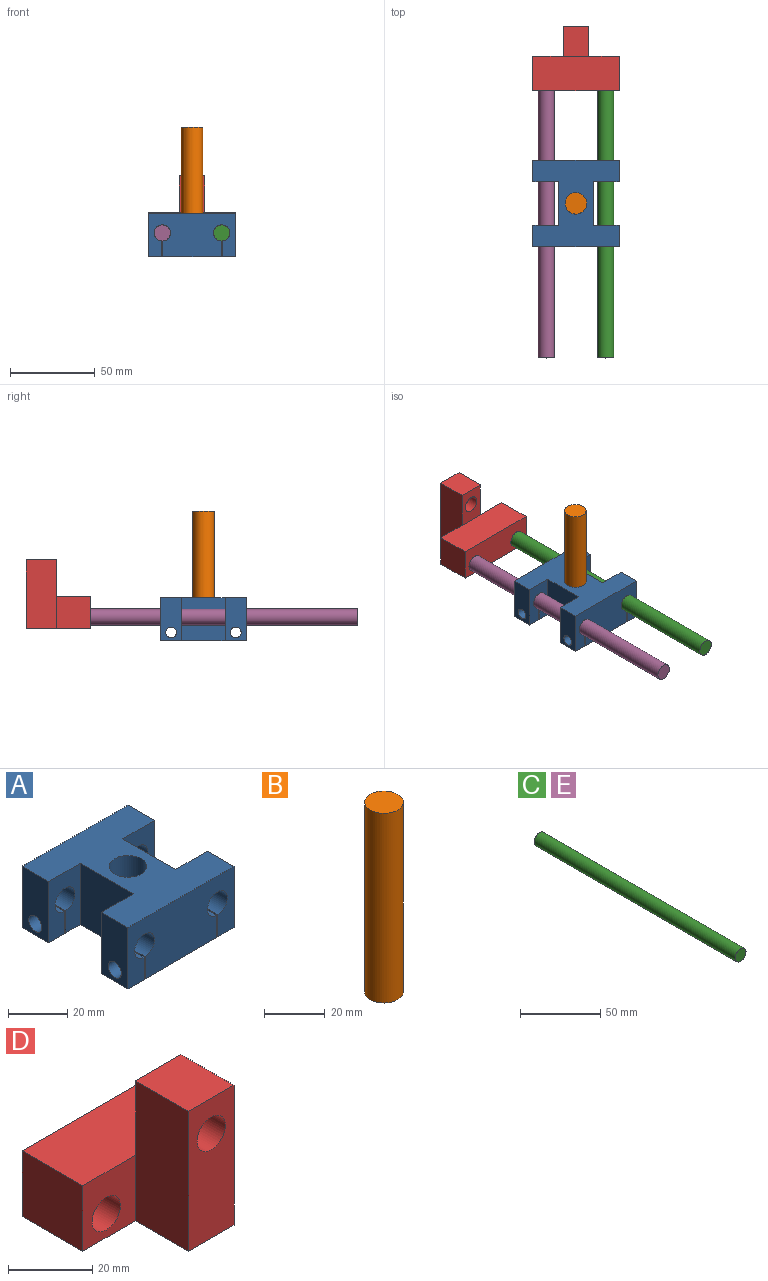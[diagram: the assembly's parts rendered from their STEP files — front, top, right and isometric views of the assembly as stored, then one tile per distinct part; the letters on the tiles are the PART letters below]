
ASSEMBLY  parts=5 mates=5
PART A: 37 faces, bbox 50.8x50.8x25.4 mm
  f0: plane 25.4x12.7mm, normal (1,0,0), area 290.9mm2, adj f8,f9,f22,f28,f36
  f1: plane 25.4x12.7mm, normal (-1,0,0), area 290.9mm2, adj f9,f20,f22,f26,f31
  f2: cylinder r=4.76mm len=12.7mm, axis (0,1,0), area 373.6mm2, adj f3,f11,f23,f27
  f3: plane 12.7x9.21mm, normal (-1,0,0), area 85.4mm2, adj f2,f4,f23,f27,f34
  f4: plane 50.8x34.42mm, normal (0,0,-1), area 1263.6mm2, adj f3,f5,f13,f14,f22,f23,f24,f25
  f5: plane 12.7x9.21mm, normal (1,0,0), area 85.4mm2, adj f4,f6,f22,f28,f35
  f6: cylinder r=4.76mm len=12.7mm, axis (0,1,0), area 373.6mm2, adj f5,f7,f22,f28
  f7: plane 12.7x9.21mm, normal (-1,0,0), area 85.4mm2, adj f6,f8,f22,f28,f36
  f8: plane 12.7x7.68mm, normal (0,0,-1), area 97.6mm2, adj f0,f7,f22,f28
  f9: plane 50.8x50.8mm, normal (0,0,1), area 1679.8mm2, adj f0,f1,f18,f19,f22,f23,f24,f25
  f10: plane 12.7x7.68mm, normal (0,0,-1), area 97.6mm2, adj f11,f19,f23,f27
  f11: plane 12.7x9.21mm, normal (1,0,0), area 85.4mm2, adj f2,f10,f23,f27,f32
  f12: cylinder r=4.76mm len=12.7mm, axis (0,1,0), area 373.6mm2, adj f13,f21,f22,f26
  f13: plane 12.7x9.21mm, normal (-1,0,0), area 85.4mm2, adj f4,f12,f22,f26,f35
  f14: plane 12.7x9.21mm, normal (1,0,0), area 85.4mm2, adj f4,f15,f23,f29,f34
  f15: cylinder r=4.76mm len=12.7mm, axis (0,1,0), area 373.6mm2, adj f14,f16,f23,f29
  f16: plane 12.7x9.21mm, normal (-1,0,0), area 85.4mm2, adj f15,f17,f23,f29,f33
  f17: plane 12.7x7.68mm, normal (0,0,-1), area 97.6mm2, adj f16,f18,f23,f29
  f18: plane 25.4x12.7mm, normal (1,0,0), area 290.9mm2, adj f9,f17,f23,f29,f33
  f19: plane 25.4x12.7mm, normal (-1,0,0), area 290.9mm2, adj f9,f10,f23,f27,f32
  f20: plane 12.7x7.68mm, normal (0,0,-1), area 97.6mm2, adj f1,f21,f22,f26
  f21: plane 12.7x9.21mm, normal (1,0,0), area 85.4mm2, adj f12,f20,f22,f26,f31
  f22: plane 50.8x25.4mm, normal (0,-1,0), area 1138.5mm2, adj f0,f1,f4,f5,f6,f7,f8,f9
  f23: plane 50.8x25.4mm, normal (0,1,0), area 1138.5mm2, adj f2,f3,f4,f9,f10,f11,f14,f15
  f24: cylinder r=6.35mm len=25.4mm, axis (0,0,1), area 1013.4mm2, adj f4,f9
  f25: plane 25.4x25.4mm, normal (-1,0,0), area 645.2mm2, adj f4,f9,f26,f27
  f26: plane 25.4x15.24mm, normal (0,1,0), area 311.2mm2, adj f1,f4,f9,f12,f13,f20,f21,f25
  f27: plane 25.4x15.24mm, normal (0,-1,0), area 311.2mm2, adj f2,f3,f4,f9,f10,f11,f19,f25
  f28: plane 25.4x15.24mm, normal (0,1,0), area 311.2mm2, adj f0,f4,f5,f6,f7,f8,f9,f30
  f29: plane 25.4x15.24mm, normal (0,-1,0), area 311.2mm2, adj f4,f9,f14,f15,f16,f17,f18,f30
  f30: plane 25.4x25.4mm, normal (1,0,0), area 645.2mm2, adj f4,f9,f28,f29
  f31: cylinder r=3.17mm len=7.68mm, axis (1,0,0), area 153.3mm2, adj f1,f21
  f32: cylinder r=3.17mm len=7.68mm, axis (1,0,0), area 153.3mm2, adj f11,f19
  f33: cylinder r=3.17mm len=7.68mm, axis (1,0,0), area 153.3mm2, adj f16,f18
  f34: cylinder r=3.17mm len=34.42mm, axis (1,0,0), area 686.6mm2, adj f3,f14
  f35: cylinder r=3.17mm len=34.42mm, axis (1,0,0), area 686.6mm2, adj f5,f13
  f36: cylinder r=3.17mm len=7.68mm, axis (1,0,0), area 153.3mm2, adj f0,f7
PART B: 3 faces, bbox 12.7x12.7x76.2 mm
  f0: cylinder r=6.35mm len=76.2mm, axis (0,0,-1), area 3040.2mm2, adj f1,f2
  f1: plane 12.7x12.7mm, normal (0,0,1), area 126.7mm2, adj f0
  f2: plane 12.7x12.7mm, normal (0,0,-1), area 126.7mm2, adj f0
PART C: 3 faces, bbox 9.5x177.8x9.5 mm
  f0: cylinder r=4.76mm len=177.8mm, axis (0,-1,0), area 5320.4mm2, adj f1,f2
  f1: plane 9.53x9.53mm, normal (0,1,0), area 71.3mm2, adj f0
  f2: plane 9.53x9.53mm, normal (0,-1,0), area 71.3mm2, adj f0
PART D: 15 faces, bbox 50.8x38.1x40.6 mm
  f0: plane 17.78x15.24mm, normal (0,0,1), area 271mm2, adj f1,f2,f11,f13
  f1: plane 40.64x15.24mm, normal (0,-1,0), area 548.1mm2, adj f0,f3,f7,f11,f13
  f2: plane 21.59x15.24mm, normal (0,1,0), area 257.8mm2, adj f0,f7,f10,f11,f13
  f3: plane 50.8x38.1mm, normal (0,0,-1), area 1303.2mm2, adj f1,f6,f8,f9,f11,f12,f13,f14
  f4: cylinder r=4.76mm len=20.32mm, axis (0,1,0), area 608mm2, adj f9,f14
  f5: cylinder r=4.76mm len=20.32mm, axis (0,1,0), area 608mm2, adj f9,f12
  f6: plane 20.32x19.05mm, normal (-1,0,0), area 387.1mm2, adj f3,f9,f10,f12
  f7: cylinder r=4.76mm len=17.78mm, axis (0,1,0), area 532mm2, adj f1,f2
  f8: plane 20.32x19.05mm, normal (1,0,0), area 387.1mm2, adj f3,f9,f10,f14
  f9: plane 50.8x19.05mm, normal (0,1,0), area 825.2mm2, adj f3,f4,f5,f6,f8,f10
  f10: plane 50.8x20.32mm, normal (0,0,1), area 1032.3mm2, adj f2,f6,f8,f9,f12,f14
  f11: plane 40.64x17.78mm, normal (-1,0,0), area 722.6mm2, adj f0,f1,f2,f3,f12
  f12: plane 19.05x17.78mm, normal (0,-1,0), area 267.5mm2, adj f3,f5,f6,f10,f11
  f13: plane 40.64x17.78mm, normal (1,0,0), area 722.6mm2, adj f0,f1,f2,f3,f14
  f14: plane 19.05x17.78mm, normal (0,-1,0), area 267.5mm2, adj f3,f4,f8,f10,f13
PART E: same geometry as C
PLACE A t=(-18.2,0,-21.24)mm
PLACE B t=(-18.2,-25.4,-43.28)mm
PLACE C t=(-0.73,-116.44,-29.31)mm
PLACE D rot(axis=(0,0,1),180deg) t=(-18.2,41.04,-14.25)mm
PLACE E t=(-35.66,-116.44,-29.31)mm
MATE fastened E.f0 <-> D.f4  axis (0,1,0) through (-35.66,61.36,-29.31)mm
MATE slider E.f0 <-> A.f2  axis (0,-1,0) through (-35.66,61.36,-29.31)mm
MATE fastened D.f5 <-> C.f0  axis (0,1,0) through (-0.73,61.36,-29.31)mm
MATE fastened B.f0 <-> A.f24  axis (0,0,-1) through (-18.2,-25.4,-43.28)mm
MATE slider C.f0 <-> A.f6  axis (0,-1,0) through (-0.73,-116.44,-29.31)mm
